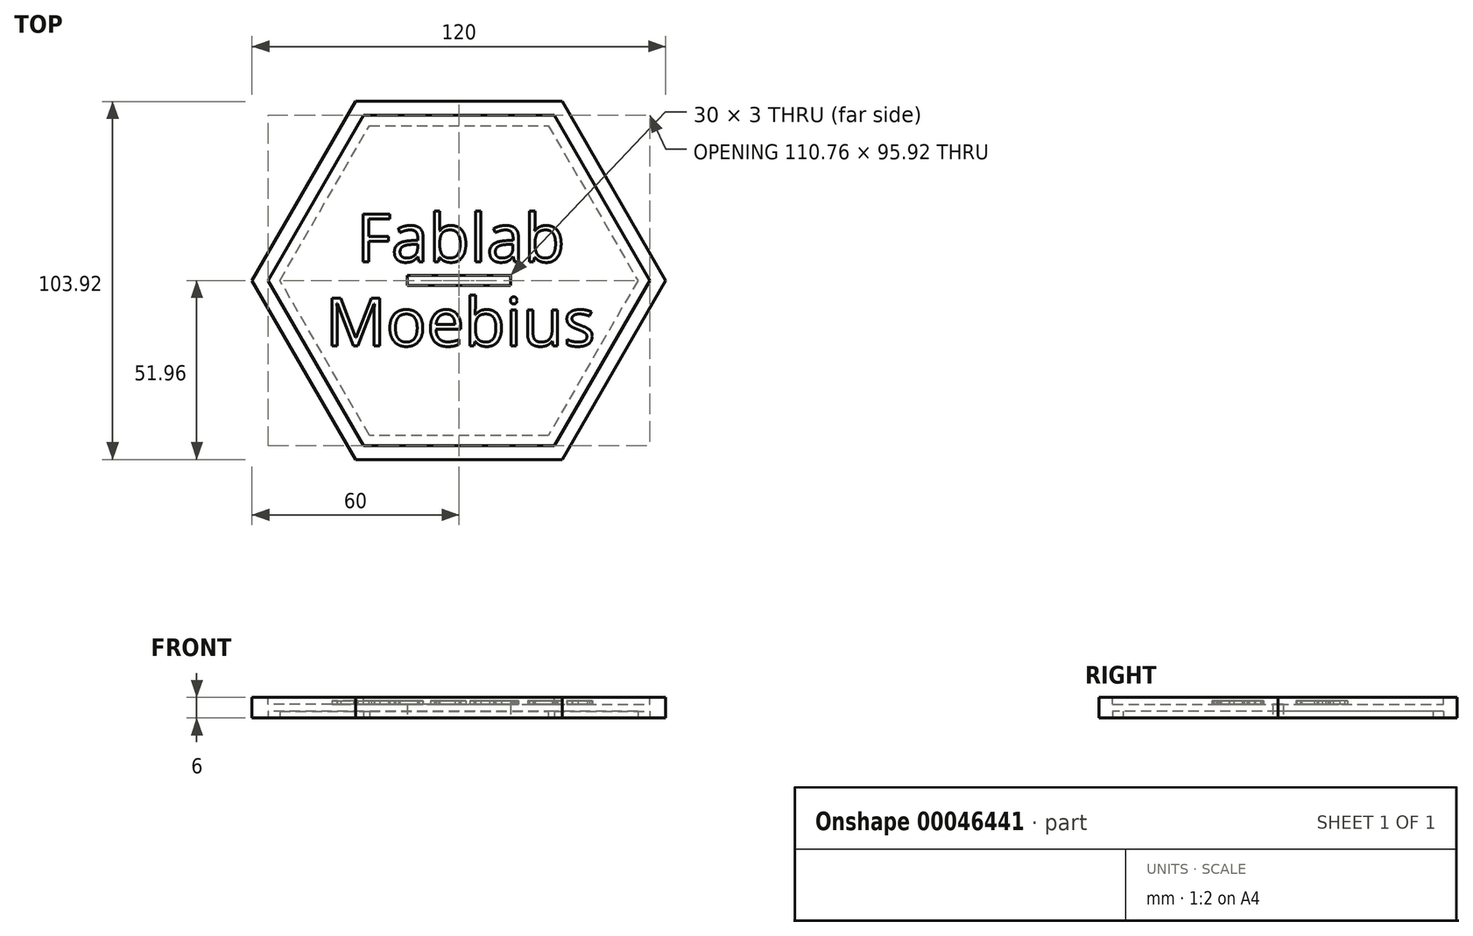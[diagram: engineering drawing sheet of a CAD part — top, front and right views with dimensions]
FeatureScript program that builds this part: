
annotation { "Feature Type Name" : "Feature", "Feature Type Description" : "" }
export const myFeature = defineFeature(function(context is Context, id is Id, definition is map)
    precondition{}
    {
        {
            var Q0;
            Q0=qCreatedBy(makeId("Top.planeOp"),FACE);
            var sketch = newSketch(context, id + "F0", { "sketchPlane" : qUnion([Q0])});
            skCircle(sketch, "E0.cCircle", {"center": v(0, 0) * mm, "radius": 60 * mm, "construction": true});
            skLineSegment(sketch, "E0.0", {"start": v(60, 0) * mm, "end": v(30, -51.96) * mm});
            skLineSegment(sketch, "E0.1", {"start": v(30, -51.96) * mm, "end": v(-30, -51.96) * mm});
            skLineSegment(sketch, "E0.2", {"start": v(-30, -51.96) * mm, "end": v(-60, 0) * mm});
            skLineSegment(sketch, "E0.3", {"start": v(-60, 0) * mm, "end": v(-30, 51.96) * mm});
            skLineSegment(sketch, "E0.4", {"start": v(-30, 51.96) * mm, "end": v(30, 51.96) * mm});
            skLineSegment(sketch, "E0.5", {"start": v(30, 51.96) * mm, "end": v(60, 0) * mm});
            skLineSegment(sketch, "E1.bottom", {"start": v(15, 1.5) * mm, "end": v(-15, 1.5) * mm});
            skLineSegment(sketch, "E1.top", {"start": v(15, -1.5) * mm, "end": v(-15, -1.5) * mm});
            skLineSegment(sketch, "E1.left", {"start": v(15, 1.5) * mm, "end": v(15, -1.5) * mm});
            skLineSegment(sketch, "E1.right", {"start": v(-15, 1.5) * mm, "end": v(-15, -1.5) * mm});
            skSolve(sketch);
        }
        {
            var Q0;
            Q0=qSketchRegion(id+"F0",true);
            var Q1;
            Q1=makeQuery(id+"F0.imprint","IMPRINT",FACE,{"disambiguationData":[TD([[makeQuery(id+"F0.imprint","IMPRINT",EDGE,{"derivedFrom":sQuery(id+"F0.wireOp",EDGE,"E0.0")}),-1.0]])]});
            extrude(context, id + "F1", {"entities" : qUnion([Q0, Q1]), "depth" : 6 * mm});
        }
        {
            var Q0;
            Q0=makeQuery(id+"F1.opExtrude","CAP_FACE",FACE,{"disambiguationData":[OSD([sQuery(id+"F0.wireOp",EDGE,"E0.0"),sQuery(id+"F0.wireOp",EDGE,"E0.1"),sQuery(id+"F0.wireOp",EDGE,"E0.2"),sQuery(id+"F0.wireOp",EDGE,"E0.3"),sQuery(id+"F0.wireOp",EDGE,"E0.4"),sQuery(id+"F0.wireOp",EDGE,"E0.5")])],"isStart":true});
            var sketch = newSketch(context, id + "F2", { "sketchPlane" : qUnion([Q0])});
            skLineSegment(sketch, "E2.0", {"start": v(27.7, -47.96) * mm, "end": v(55.38, 0) * mm});
            skLineSegment(sketch, "E2.1", {"start": v(27.7, 47.96) * mm, "end": v(-27.7, 47.96) * mm});
            skLineSegment(sketch, "E2.2", {"start": v(-27.7, 47.96) * mm, "end": v(-55.38, 0) * mm});
            skLineSegment(sketch, "E2.3", {"start": v(55.38, 0) * mm, "end": v(27.7, 47.96) * mm});
            skLineSegment(sketch, "E2.4", {"start": v(-55.38, 0) * mm, "end": v(-27.7, -47.96) * mm});
            skLineSegment(sketch, "E2.5", {"start": v(-27.7, -47.96) * mm, "end": v(27.7, -47.96) * mm});
            skLineSegment(sketch, "E3.0", {"start": v(25.96, -44.96) * mm, "end": v(51.92, 0) * mm});
            skLineSegment(sketch, "E3.1", {"start": v(25.96, 44.96) * mm, "end": v(-25.96, 44.96) * mm});
            skLineSegment(sketch, "E3.2", {"start": v(-25.96, 44.96) * mm, "end": v(-51.92, 0) * mm});
            skLineSegment(sketch, "E3.3", {"start": v(51.92, 0) * mm, "end": v(25.96, 44.96) * mm});
            skLineSegment(sketch, "E3.4", {"start": v(-51.92, 0) * mm, "end": v(-25.96, -44.96) * mm});
            skLineSegment(sketch, "E3.5", {"start": v(-25.96, -44.96) * mm, "end": v(25.96, -44.96) * mm});
            skSolve(sketch);
        }
        {
            var Q0;
            Q0=qSketchRegion(id+"F2",true);
            extrude(context, id + "F3", {"entities" : qUnion([Q0]), "operationType" : NewBodyOperationType.REMOVE, "oppositeDirection" : true, "depth" : 2 * mm});
        }
        {
            var Q0;
            Q0=makeQuery(id+"F1.opExtrude","CAP_FACE",FACE,{"disambiguationData":[OSD([sQuery(id+"F0.wireOp",EDGE,"E0.0"),sQuery(id+"F0.wireOp",EDGE,"E0.1"),sQuery(id+"F0.wireOp",EDGE,"E0.2"),sQuery(id+"F0.wireOp",EDGE,"E0.3"),sQuery(id+"F0.wireOp",EDGE,"E0.4"),sQuery(id+"F0.wireOp",EDGE,"E0.5")])],"isStart":false});
            var sketch = newSketch(context, id + "F4", { "sketchPlane" : qUnion([Q0])});
            skLineSegment(sketch, "E4.0", {"start": v(-27.7, -47.96) * mm, "end": v(27.7, -47.96) * mm});
            skLineSegment(sketch, "E4.1", {"start": v(55.38, 0) * mm, "end": v(27.7, 47.96) * mm});
            skLineSegment(sketch, "E4.2", {"start": v(27.7, 47.96) * mm, "end": v(-27.7, 47.96) * mm});
            skLineSegment(sketch, "E4.3", {"start": v(27.7, -47.96) * mm, "end": v(55.38, 0) * mm});
            skLineSegment(sketch, "E4.4", {"start": v(-27.7, 47.96) * mm, "end": v(-55.38, 0) * mm});
            skLineSegment(sketch, "E4.5", {"start": v(-55.38, 0) * mm, "end": v(-27.7, -47.96) * mm});
            skSolve(sketch);
        }
        {
            var Q0;
            Q0=makeQuery(id+"F4.imprint","IMPRINT",FACE,{"disambiguationData":[TD([[makeQuery(id+"F4.imprint","IMPRINT",EDGE,{"derivedFrom":sQuery(id+"F4.wireOp",EDGE,"E4.0")}),1.0]])]});
            extrude(context, id + "F5", {"entities" : qUnion([Q0]), "operationType" : NewBodyOperationType.REMOVE, "oppositeDirection" : true, "depth" : 2 * mm});
        }
        {
            var Q0;
            Q0=makeQuery(id+"F5.boolean.opBoolean","COPY",FACE,{"derivedFrom":makeQuery(id+"F5.opExtrude","CAP_FACE",FACE,{"disambiguationData":[OSD([sQuery(id+"F4.wireOp",EDGE,"E4.0"),sQuery(id+"F4.wireOp",EDGE,"E4.1"),sQuery(id+"F4.wireOp",EDGE,"E4.2"),sQuery(id+"F4.wireOp",EDGE,"E4.3"),sQuery(id+"F4.wireOp",EDGE,"E4.4"),sQuery(id+"F4.wireOp",EDGE,"E4.5")])],"isStart":false})});
            var sketch = newSketch(context, id + "F6", { "sketchPlane" : qUnion([Q0])});
            skText(sketch, "E5", { "text": "Moebius", "fontName": "OpenSans-Regular.ttf"});
            skText(sketch, "E6", { "text": "Fablab", "fontName": "OpenSans-Regular.ttf"});
            const initialGuessF6  = {"E5": [-0.03868, -0.019, 1, 0, 0.014], "E6": [-0.02966, 0.0054, 1, 0, 0.014]};
            skSetInitialGuess(sketch, initialGuessF6);
            skSolve(sketch);
        }
        {
            var Q0;
            Q0=qSketchRegion(id+"F6",true);
            extrude(context, id + "F7", {"entities" : qUnion([Q0]), "operationType" : NewBodyOperationType.ADD, "depth" : 1 * mm});
        }
    });
